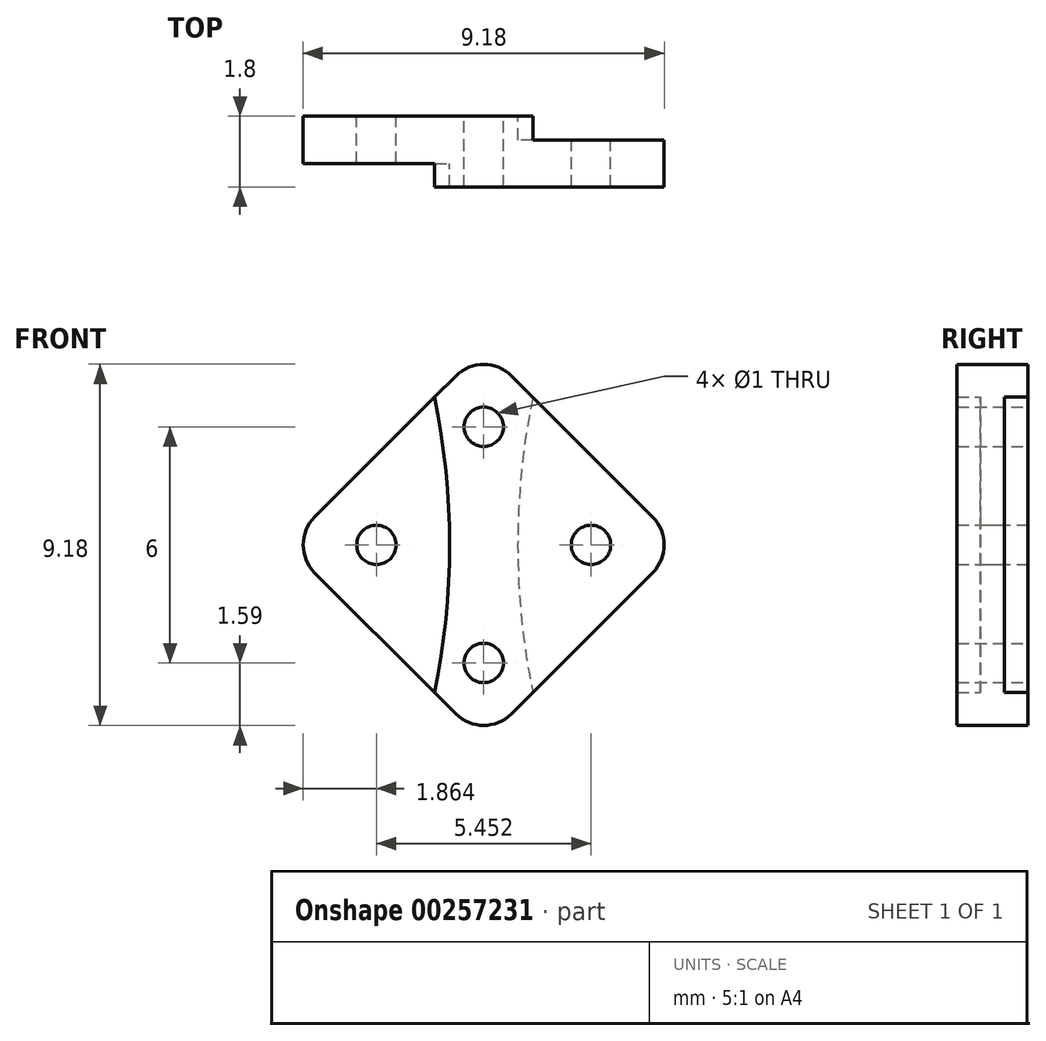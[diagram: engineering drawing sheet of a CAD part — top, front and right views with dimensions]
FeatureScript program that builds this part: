
annotation { "Feature Type Name" : "Feature", "Feature Type Description" : "" }
export const myFeature = defineFeature(function(context is Context, id is Id, definition is map)
    precondition{}
    {
        {
            var Q0;
            Q0=qCreatedBy(makeId("Front.planeOp"),FACE);
            var sketch = newSketch(context, id + "F0", { "sketchPlane" : qUnion([Q0])});
            skLineSegment(sketch, "E0", {"start": v(0, 5) * mm, "end": v(-5, 0) * mm});
            skLineSegment(sketch, "E1", {"start": v(-5, 0) * mm, "end": v(0, -5) * mm});
            skLineSegment(sketch, "E2", {"start": v(0, -5) * mm, "end": v(5, 0) * mm});
            skLineSegment(sketch, "E3", {"start": v(5, 0) * mm, "end": v(0, 5) * mm});
            skArc(sketch, "E4", {"start": v(0, -5) * mm, "mid": v(0.64, 0) * mm, "end": v(0, 5) * mm, "construction": true});
            skArc(sketch, "E5.0", {"start": v(-1.25, -3.75) * mm, "mid": v(-0.86, 0) * mm, "end": v(-1.25, 3.75) * mm});
            skSolve(sketch);
        }
        {
            var Q0;
            Q0=makeQuery(id+"F0.imprint","IMPRINT",FACE,{"disambiguationData":[TD([[makeQuery(id+"F0.imprint","IMPRINT",EDGE,{"derivedFrom":sQuery(id+"F0.wireOp",EDGE,"E2")}),1.0]])]});
            extrude(context, id + "F1", {"entities" : qUnion([Q0]), "depth" : 1.8 * mm});
        }
        {
            var Q0;
            Q0=makeQuery(id+"F0.imprint","IMPRINT",FACE,{"disambiguationData":[TD([[makeQuery(id+"F0.imprint","IMPRINT",EDGE,{"derivedFrom":sQuery(id+"F0.wireOp",EDGE,"E0")}),1.0]])]});
            extrude(context, id + "F2", {"entities" : qUnion([Q0]), "operationType" : NewBodyOperationType.ADD, "depth" : 1.2 * mm});
        }
        {
            var Q0;
            {var subQ1=sQuery(id+"F0.wireOp",EDGE,"E2");Q0=makeQuery(id+"F0.imprint","IMPRINT",FACE,{"disambiguationData":[TD([[makeQuery(id+"F0.imprint","IMPRINT",EDGE,{"derivedFrom":subQ1}),1.0]])]});}
            var sketch = newSketch(context, id + "F3", { "sketchPlane" : qUnion([Q0])});
            skPoint(sketch, "E6.0", {"position": v(0, 5) * mm});
            skPoint(sketch, "E7.0", {"position": v(0, -5) * mm});
            skLineSegment(sketch, "E8", {"start": v(0, 5) * mm, "end": v(0, -5) * mm, "construction": true});
            skArc(sketch, "E9.0", {"start": v(-1.25, -3.75) * mm, "mid": v(-0.86, 0) * mm, "end": v(-1.25, 3.75) * mm, "construction": true});
            skArc(sketch, "E10.MirrorCS", {"start": v(1.25, -3.75) * mm, "mid": v(0.86, 0) * mm, "end": v(1.25, 3.75) * mm});
            skLineSegment(sketch, "E11.0", {"start": v(5, 0) * mm, "end": v(1.25, 3.75) * mm});
            skLineSegment(sketch, "E12.0", {"start": v(1.25, -3.75) * mm, "end": v(5, 0) * mm});
            skSolve(sketch);
        }
        {
            var Q0;
            Q0 = qSketchRegion(id + "F3", true);
            extrude(context, id + "F4", {"entities" : qUnion([Q0]), "operationType" : NewBodyOperationType.REMOVE, "depth" : .6 * mm});
        }
        {
            var Q0;
            Q0=makeQuery(id+"F1.opExtrude","SWEPT_EDGE",EDGE,{"disambiguationData":[OSD([sQuery(id+"F0.wireOp",EDGE,"E0"),sQuery(id+"F0.wireOp",EDGE,"E3")])]});
            var Q1;
            Q1=makeQuery(id+"F1.opExtrude","SWEPT_EDGE",EDGE,{"disambiguationData":[OSD([sQuery(id+"F0.wireOp",EDGE,"E2"),sQuery(id+"F0.wireOp",EDGE,"E3")])]});
            var Q2;
            Q2=makeQuery(id+"F1.opExtrude","SWEPT_EDGE",EDGE,{"disambiguationData":[OSD([sQuery(id+"F0.wireOp",EDGE,"E1"),sQuery(id+"F0.wireOp",EDGE,"E2")])]});
            var Q3;
            Q3=makeQuery(id+"F2.opExtrude","SWEPT_EDGE",EDGE,{"disambiguationData":[OSD([sQuery(id+"F0.wireOp",EDGE,"E0"),sQuery(id+"F0.wireOp",EDGE,"E1")])]});
            fillet(context, id + "F5", {"entities" : qUnion([Q0, Q1, Q2, Q3]), "radius" : 1 * mm, "tangentPropagation" : true, "allowEdgeOverflow" : false});
        }
        {
            var Q0;
            Q0=qCreatedBy(makeId("Front.planeOp"),FACE);
            var sketch = newSketch(context, id + "F6", { "sketchPlane" : qUnion([Q0])});
            skCircle(sketch, "E13", {"center": v(-2.73, 0) * mm, "radius": 0.5 * mm});
            skCircle(sketch, "E14", {"center": v(2.73, 0) * mm, "radius": 0.5 * mm});
            skCircle(sketch, "E15", {"center": v(0, 3) * mm, "radius": 0.5 * mm});
            skCircle(sketch, "E16", {"center": v(0, -3) * mm, "radius": 0.5 * mm});
            skArc(sketch, "E17.0", {"start": v(1.25, -3.75) * mm, "mid": v(0.86, 0) * mm, "end": v(1.25, 3.75) * mm, "construction": true});
            skArc(sketch, "E18.0", {"start": v(4.3, 0.7) * mm, "mid": v(4.59, 0) * mm, "end": v(4.3, -0.7) * mm, "construction": true});
            skArc(sketch, "E19.0", {"start": v(-1.25, -3.75) * mm, "mid": v(-0.86, 0) * mm, "end": v(-1.25, 3.75) * mm, "construction": true});
            skArc(sketch, "E20.0", {"start": v(-4.3, -0.7) * mm, "mid": v(-4.59, 0) * mm, "end": v(-4.3, 0.7) * mm, "construction": true});
            skSolve(sketch);
        }
        {
            var Q0;
            Q0 = qSketchRegion(id + "F6", true);
            extrude(context, id + "F7", {"entities" : qUnion([Q0]), "operationType" : NewBodyOperationType.REMOVE, "endBound" : BoundingType.SYMMETRIC, "depth" : 25 * mm});
        }
    });
